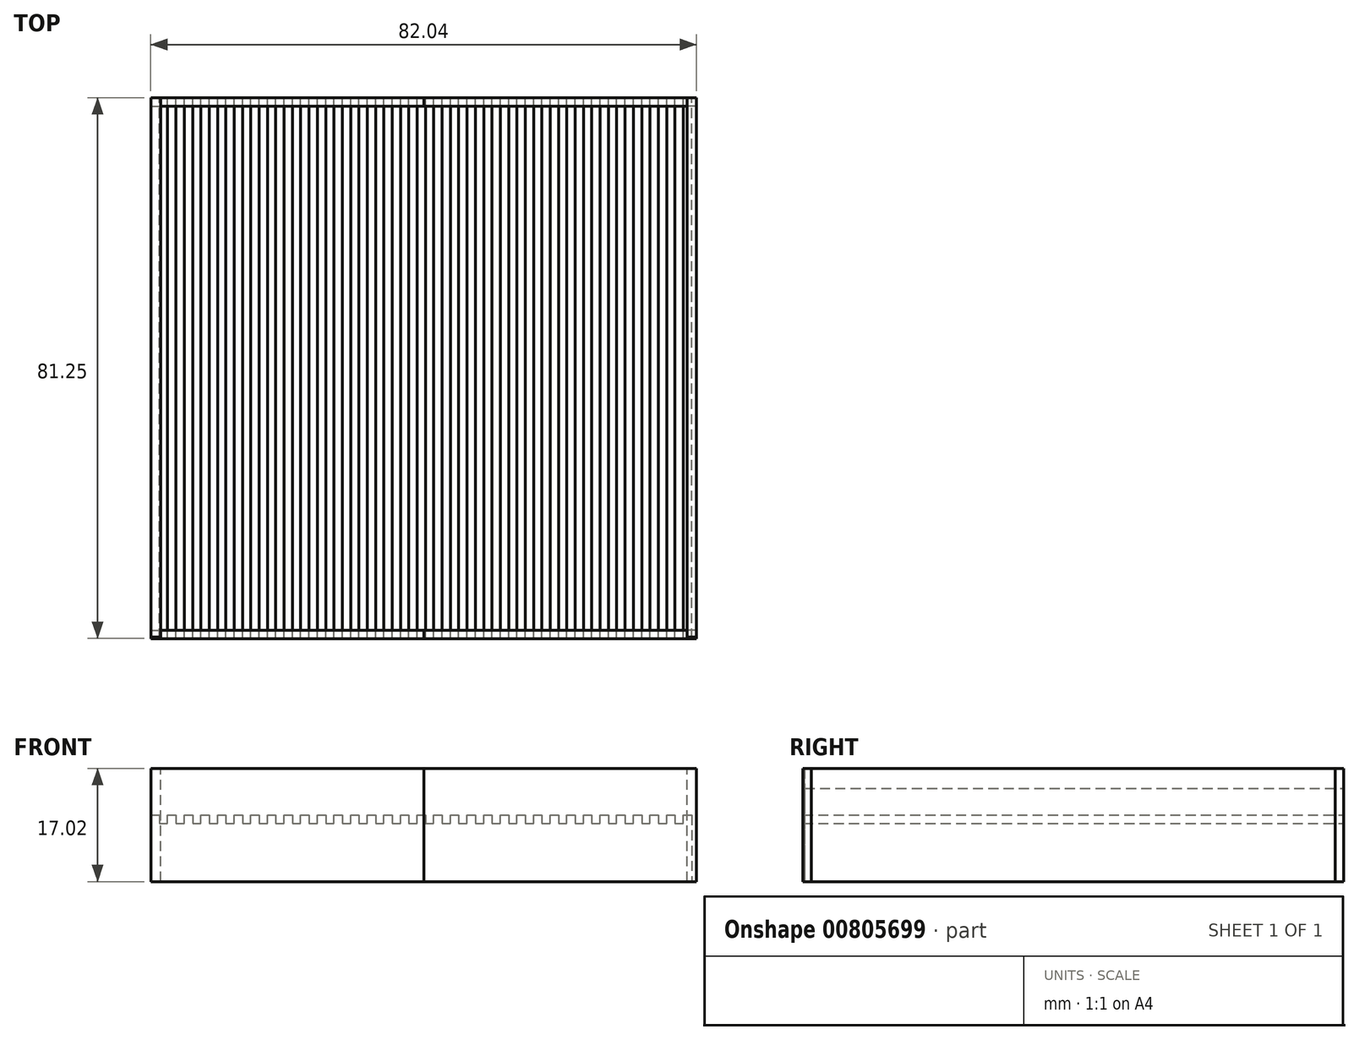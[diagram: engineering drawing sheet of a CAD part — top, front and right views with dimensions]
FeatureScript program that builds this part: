
annotation { "Feature Type Name" : "Feature", "Feature Type Description" : "" }
export const myFeature = defineFeature(function(context is Context, id is Id, definition is map)
    precondition{}
    {
        {
            var Q0;
            Q0=qCreatedBy(makeId("Front.planeOp"),FACE);
            var sketch = newSketch(context, id + "F0", { "sketchPlane" : qUnion([Q0])});
            skLineSegment(sketch, "E0.top", {"start": v(-41, -5) * mm, "end": v(40.25, -5) * mm});
            skLineSegment(sketch, "E0.left", {"start": v(-41, 5) * mm, "end": v(-41, -5) * mm});
            skLineSegment(sketch, "E0.right", {"start": v(40.25, 3.75) * mm, "end": v(40.25, -5) * mm});
            skLineSegment(sketch, "E1", {"start": v(-41, 5) * mm, "end": v(-39.75, 5) * mm});
            skLineSegment(sketch, "E2", {"start": v(-39.75, 5) * mm, "end": v(-39.75, 3.75) * mm});
            skLineSegment(sketch, "E3", {"start": v(-39.75, 3.75) * mm, "end": v(-38.5, 3.75) * mm});
            skLineSegment(sketch, "E4", {"start": v(-38.5, 3.75) * mm, "end": v(-38.5, 5) * mm});
            skLineSegment(sketch, "E5.1.0.0", {"start": v(-36, 3.75) * mm, "end": v(-36, 5) * mm});
            skLineSegment(sketch, "E5.1.0.1", {"start": v(-37.25, 3.75) * mm, "end": v(-36, 3.75) * mm});
            skLineSegment(sketch, "E5.1.0.2", {"start": v(-37.25, 5) * mm, "end": v(-37.25, 3.75) * mm});
            skLineSegment(sketch, "E5.1.0.3", {"start": v(-38.5, 5) * mm, "end": v(-37.25, 5) * mm});
            skLineSegment(sketch, "E5.2.0.0", {"start": v(-33.5, 3.75) * mm, "end": v(-33.5, 5) * mm});
            skLineSegment(sketch, "E5.2.0.1", {"start": v(-34.75, 3.75) * mm, "end": v(-33.5, 3.75) * mm});
            skLineSegment(sketch, "E5.2.0.2", {"start": v(-34.75, 5) * mm, "end": v(-34.75, 3.75) * mm});
            skLineSegment(sketch, "E5.2.0.3", {"start": v(-36, 5) * mm, "end": v(-34.75, 5) * mm});
            skLineSegment(sketch, "E5.3.0.0", {"start": v(-31, 3.75) * mm, "end": v(-31, 5) * mm});
            skLineSegment(sketch, "E5.3.0.1", {"start": v(-32.25, 3.75) * mm, "end": v(-31, 3.75) * mm});
            skLineSegment(sketch, "E5.3.0.2", {"start": v(-32.25, 5) * mm, "end": v(-32.25, 3.75) * mm});
            skLineSegment(sketch, "E5.3.0.3", {"start": v(-33.5, 5) * mm, "end": v(-32.25, 5) * mm});
            skLineSegment(sketch, "E5.4.0.0", {"start": v(-28.5, 3.75) * mm, "end": v(-28.5, 5) * mm});
            skLineSegment(sketch, "E5.4.0.1", {"start": v(-29.75, 3.75) * mm, "end": v(-28.5, 3.75) * mm});
            skLineSegment(sketch, "E5.4.0.2", {"start": v(-29.75, 5) * mm, "end": v(-29.75, 3.75) * mm});
            skLineSegment(sketch, "E5.4.0.3", {"start": v(-31, 5) * mm, "end": v(-29.75, 5) * mm});
            skLineSegment(sketch, "E5.5.0.0", {"start": v(-26, 3.75) * mm, "end": v(-26, 5) * mm});
            skLineSegment(sketch, "E5.5.0.1", {"start": v(-27.25, 3.75) * mm, "end": v(-26, 3.75) * mm});
            skLineSegment(sketch, "E5.5.0.2", {"start": v(-27.25, 5) * mm, "end": v(-27.25, 3.75) * mm});
            skLineSegment(sketch, "E5.5.0.3", {"start": v(-28.5, 5) * mm, "end": v(-27.25, 5) * mm});
            skLineSegment(sketch, "E5.6.0.0", {"start": v(-23.5, 3.75) * mm, "end": v(-23.5, 5) * mm});
            skLineSegment(sketch, "E5.6.0.1", {"start": v(-24.75, 3.75) * mm, "end": v(-23.5, 3.75) * mm});
            skLineSegment(sketch, "E5.6.0.2", {"start": v(-24.75, 5) * mm, "end": v(-24.75, 3.75) * mm});
            skLineSegment(sketch, "E5.6.0.3", {"start": v(-26, 5) * mm, "end": v(-24.75, 5) * mm});
            skLineSegment(sketch, "E5.7.0.0", {"start": v(-21, 3.75) * mm, "end": v(-21, 5) * mm});
            skLineSegment(sketch, "E5.7.0.1", {"start": v(-22.25, 3.75) * mm, "end": v(-21, 3.75) * mm});
            skLineSegment(sketch, "E5.7.0.2", {"start": v(-22.25, 5) * mm, "end": v(-22.25, 3.75) * mm});
            skLineSegment(sketch, "E5.7.0.3", {"start": v(-23.5, 5) * mm, "end": v(-22.25, 5) * mm});
            skLineSegment(sketch, "E5.8.0.0", {"start": v(-18.5, 3.75) * mm, "end": v(-18.5, 5) * mm});
            skLineSegment(sketch, "E5.8.0.1", {"start": v(-19.75, 3.75) * mm, "end": v(-18.5, 3.75) * mm});
            skLineSegment(sketch, "E5.8.0.2", {"start": v(-19.75, 5) * mm, "end": v(-19.75, 3.75) * mm});
            skLineSegment(sketch, "E5.8.0.3", {"start": v(-21, 5) * mm, "end": v(-19.75, 5) * mm});
            skLineSegment(sketch, "E5.9.0.0", {"start": v(-16, 3.75) * mm, "end": v(-16, 5) * mm});
            skLineSegment(sketch, "E5.9.0.1", {"start": v(-17.25, 3.75) * mm, "end": v(-16, 3.75) * mm});
            skLineSegment(sketch, "E5.9.0.2", {"start": v(-17.25, 5) * mm, "end": v(-17.25, 3.75) * mm});
            skLineSegment(sketch, "E5.9.0.3", {"start": v(-18.5, 5) * mm, "end": v(-17.25, 5) * mm});
            skLineSegment(sketch, "E5.10.0.0", {"start": v(-13.5, 3.75) * mm, "end": v(-13.5, 5) * mm});
            skLineSegment(sketch, "E5.10.0.1", {"start": v(-14.75, 3.75) * mm, "end": v(-13.5, 3.75) * mm});
            skLineSegment(sketch, "E5.10.0.2", {"start": v(-14.75, 5) * mm, "end": v(-14.75, 3.75) * mm});
            skLineSegment(sketch, "E5.10.0.3", {"start": v(-16, 5) * mm, "end": v(-14.75, 5) * mm});
            skLineSegment(sketch, "E5.11.0.0", {"start": v(-11, 3.75) * mm, "end": v(-11, 5) * mm});
            skLineSegment(sketch, "E5.11.0.1", {"start": v(-12.25, 3.75) * mm, "end": v(-11, 3.75) * mm});
            skLineSegment(sketch, "E5.11.0.2", {"start": v(-12.25, 5) * mm, "end": v(-12.25, 3.75) * mm});
            skLineSegment(sketch, "E5.11.0.3", {"start": v(-13.5, 5) * mm, "end": v(-12.25, 5) * mm});
            skLineSegment(sketch, "E5.12.0.0", {"start": v(-8.5, 3.75) * mm, "end": v(-8.5, 5) * mm});
            skLineSegment(sketch, "E5.12.0.1", {"start": v(-9.75, 3.75) * mm, "end": v(-8.5, 3.75) * mm});
            skLineSegment(sketch, "E5.12.0.2", {"start": v(-9.75, 5) * mm, "end": v(-9.75, 3.75) * mm});
            skLineSegment(sketch, "E5.12.0.3", {"start": v(-11, 5) * mm, "end": v(-9.75, 5) * mm});
            skLineSegment(sketch, "E5.13.0.0", {"start": v(-6, 3.75) * mm, "end": v(-6, 5) * mm});
            skLineSegment(sketch, "E5.13.0.1", {"start": v(-7.25, 3.75) * mm, "end": v(-6, 3.75) * mm});
            skLineSegment(sketch, "E5.13.0.2", {"start": v(-7.25, 5) * mm, "end": v(-7.25, 3.75) * mm});
            skLineSegment(sketch, "E5.13.0.3", {"start": v(-8.5, 5) * mm, "end": v(-7.25, 5) * mm});
            skLineSegment(sketch, "E5.14.0.0", {"start": v(-3.5, 3.75) * mm, "end": v(-3.5, 5) * mm});
            skLineSegment(sketch, "E5.14.0.1", {"start": v(-4.75, 3.75) * mm, "end": v(-3.5, 3.75) * mm});
            skLineSegment(sketch, "E5.14.0.2", {"start": v(-4.75, 5) * mm, "end": v(-4.75, 3.75) * mm});
            skLineSegment(sketch, "E5.14.0.3", {"start": v(-6, 5) * mm, "end": v(-4.75, 5) * mm});
            skLineSegment(sketch, "E5.15.0.0", {"start": v(-1, 3.75) * mm, "end": v(-1, 5) * mm});
            skLineSegment(sketch, "E5.15.0.1", {"start": v(-2.25, 3.75) * mm, "end": v(-1, 3.75) * mm});
            skLineSegment(sketch, "E5.15.0.2", {"start": v(-2.25, 5) * mm, "end": v(-2.25, 3.75) * mm});
            skLineSegment(sketch, "E5.15.0.3", {"start": v(-3.5, 5) * mm, "end": v(-2.25, 5) * mm});
            skLineSegment(sketch, "E5.16.0.0", {"start": v(1.5, 3.75) * mm, "end": v(1.5, 5) * mm});
            skLineSegment(sketch, "E5.16.0.1", {"start": v(0.25, 3.75) * mm, "end": v(1.5, 3.75) * mm});
            skLineSegment(sketch, "E5.16.0.2", {"start": v(0.25, 5) * mm, "end": v(0.25, 3.75) * mm});
            skLineSegment(sketch, "E5.16.0.3", {"start": v(-1, 5) * mm, "end": v(0.25, 5) * mm});
            skLineSegment(sketch, "E5.17.0.0", {"start": v(4, 3.75) * mm, "end": v(4, 5) * mm});
            skLineSegment(sketch, "E5.17.0.1", {"start": v(2.75, 3.75) * mm, "end": v(4, 3.75) * mm});
            skLineSegment(sketch, "E5.17.0.2", {"start": v(2.75, 5) * mm, "end": v(2.75, 3.75) * mm});
            skLineSegment(sketch, "E5.17.0.3", {"start": v(1.5, 5) * mm, "end": v(2.75, 5) * mm});
            skLineSegment(sketch, "E5.18.0.0", {"start": v(6.5, 3.75) * mm, "end": v(6.5, 5) * mm});
            skLineSegment(sketch, "E5.18.0.1", {"start": v(5.25, 3.75) * mm, "end": v(6.5, 3.75) * mm});
            skLineSegment(sketch, "E5.18.0.2", {"start": v(5.25, 5) * mm, "end": v(5.25, 3.75) * mm});
            skLineSegment(sketch, "E5.18.0.3", {"start": v(4, 5) * mm, "end": v(5.25, 5) * mm});
            skLineSegment(sketch, "E5.19.0.0", {"start": v(9, 3.75) * mm, "end": v(9, 5) * mm});
            skLineSegment(sketch, "E5.19.0.1", {"start": v(7.75, 3.75) * mm, "end": v(9, 3.75) * mm});
            skLineSegment(sketch, "E5.19.0.2", {"start": v(7.75, 5) * mm, "end": v(7.75, 3.75) * mm});
            skLineSegment(sketch, "E5.19.0.3", {"start": v(6.5, 5) * mm, "end": v(7.75, 5) * mm});
            skLineSegment(sketch, "E5.20.0.0", {"start": v(11.5, 3.75) * mm, "end": v(11.5, 5) * mm});
            skLineSegment(sketch, "E5.20.0.1", {"start": v(10.25, 3.75) * mm, "end": v(11.5, 3.75) * mm});
            skLineSegment(sketch, "E5.20.0.2", {"start": v(10.25, 5) * mm, "end": v(10.25, 3.75) * mm});
            skLineSegment(sketch, "E5.20.0.3", {"start": v(9, 5) * mm, "end": v(10.25, 5) * mm});
            skLineSegment(sketch, "E5.21.0.0", {"start": v(14, 3.75) * mm, "end": v(14, 5) * mm});
            skLineSegment(sketch, "E5.21.0.1", {"start": v(12.75, 3.75) * mm, "end": v(14, 3.75) * mm});
            skLineSegment(sketch, "E5.21.0.2", {"start": v(12.75, 5) * mm, "end": v(12.75, 3.75) * mm});
            skLineSegment(sketch, "E5.21.0.3", {"start": v(11.5, 5) * mm, "end": v(12.75, 5) * mm});
            skLineSegment(sketch, "E5.22.0.0", {"start": v(16.5, 3.75) * mm, "end": v(16.5, 5) * mm});
            skLineSegment(sketch, "E5.22.0.1", {"start": v(15.25, 3.75) * mm, "end": v(16.5, 3.75) * mm});
            skLineSegment(sketch, "E5.22.0.2", {"start": v(15.25, 5) * mm, "end": v(15.25, 3.75) * mm});
            skLineSegment(sketch, "E5.22.0.3", {"start": v(14, 5) * mm, "end": v(15.25, 5) * mm});
            skLineSegment(sketch, "E5.23.0.0", {"start": v(19, 3.75) * mm, "end": v(19, 5) * mm});
            skLineSegment(sketch, "E5.23.0.1", {"start": v(17.75, 3.75) * mm, "end": v(19, 3.75) * mm});
            skLineSegment(sketch, "E5.23.0.2", {"start": v(17.75, 5) * mm, "end": v(17.75, 3.75) * mm});
            skLineSegment(sketch, "E5.23.0.3", {"start": v(16.5, 5) * mm, "end": v(17.75, 5) * mm});
            skLineSegment(sketch, "E5.24.0.0", {"start": v(21.5, 3.75) * mm, "end": v(21.5, 5) * mm});
            skLineSegment(sketch, "E5.24.0.1", {"start": v(20.25, 3.75) * mm, "end": v(21.5, 3.75) * mm});
            skLineSegment(sketch, "E5.24.0.2", {"start": v(20.25, 5) * mm, "end": v(20.25, 3.75) * mm});
            skLineSegment(sketch, "E5.24.0.3", {"start": v(19, 5) * mm, "end": v(20.25, 5) * mm});
            skLineSegment(sketch, "E5.25.0.0", {"start": v(24, 3.75) * mm, "end": v(24, 5) * mm});
            skLineSegment(sketch, "E5.25.0.1", {"start": v(22.75, 3.75) * mm, "end": v(24, 3.75) * mm});
            skLineSegment(sketch, "E5.25.0.2", {"start": v(22.75, 5) * mm, "end": v(22.75, 3.75) * mm});
            skLineSegment(sketch, "E5.25.0.3", {"start": v(21.5, 5) * mm, "end": v(22.75, 5) * mm});
            skLineSegment(sketch, "E5.26.0.0", {"start": v(26.5, 3.75) * mm, "end": v(26.5, 5) * mm});
            skLineSegment(sketch, "E5.26.0.1", {"start": v(25.25, 3.75) * mm, "end": v(26.5, 3.75) * mm});
            skLineSegment(sketch, "E5.26.0.2", {"start": v(25.25, 5) * mm, "end": v(25.25, 3.75) * mm});
            skLineSegment(sketch, "E5.26.0.3", {"start": v(24, 5) * mm, "end": v(25.25, 5) * mm});
            skLineSegment(sketch, "E5.27.0.0", {"start": v(29, 3.75) * mm, "end": v(29, 5) * mm});
            skLineSegment(sketch, "E5.27.0.1", {"start": v(27.75, 3.75) * mm, "end": v(29, 3.75) * mm});
            skLineSegment(sketch, "E5.27.0.2", {"start": v(27.75, 5) * mm, "end": v(27.75, 3.75) * mm});
            skLineSegment(sketch, "E5.27.0.3", {"start": v(26.5, 5) * mm, "end": v(27.75, 5) * mm});
            skLineSegment(sketch, "E5.28.0.0", {"start": v(31.5, 3.75) * mm, "end": v(31.5, 5) * mm});
            skLineSegment(sketch, "E5.28.0.1", {"start": v(30.25, 3.75) * mm, "end": v(31.5, 3.75) * mm});
            skLineSegment(sketch, "E5.28.0.2", {"start": v(30.25, 5) * mm, "end": v(30.25, 3.75) * mm});
            skLineSegment(sketch, "E5.28.0.3", {"start": v(29, 5) * mm, "end": v(30.25, 5) * mm});
            skLineSegment(sketch, "E5.29.0.0", {"start": v(34, 3.75) * mm, "end": v(34, 5) * mm});
            skLineSegment(sketch, "E5.29.0.1", {"start": v(32.75, 3.75) * mm, "end": v(34, 3.75) * mm});
            skLineSegment(sketch, "E5.29.0.2", {"start": v(32.75, 5) * mm, "end": v(32.75, 3.75) * mm});
            skLineSegment(sketch, "E5.29.0.3", {"start": v(31.5, 5) * mm, "end": v(32.75, 5) * mm});
            skLineSegment(sketch, "E5.30.0.0", {"start": v(36.5, 3.75) * mm, "end": v(36.5, 5) * mm});
            skLineSegment(sketch, "E5.30.0.1", {"start": v(35.25, 3.75) * mm, "end": v(36.5, 3.75) * mm});
            skLineSegment(sketch, "E5.30.0.2", {"start": v(35.25, 5) * mm, "end": v(35.25, 3.75) * mm});
            skLineSegment(sketch, "E5.30.0.3", {"start": v(34, 5) * mm, "end": v(35.25, 5) * mm});
            skLineSegment(sketch, "E5.31.0.0", {"start": v(39, 3.75) * mm, "end": v(39, 5) * mm});
            skLineSegment(sketch, "E5.31.0.1", {"start": v(37.75, 3.75) * mm, "end": v(39, 3.75) * mm});
            skLineSegment(sketch, "E5.31.0.2", {"start": v(37.75, 5) * mm, "end": v(37.75, 3.75) * mm});
            skLineSegment(sketch, "E5.31.0.3", {"start": v(36.5, 5) * mm, "end": v(37.75, 5) * mm});
            skLineSegment(sketch, "E5.direction1", {"start": v(-38.5, 3.75) * mm, "end": v(-36, 3.75) * mm, "construction": true});
            skLineSegment(sketch, "E6.3.32.0", {"start": v(40.25, 3.75) * mm, "end": v(40.25, 3.75) * mm});
            skLineSegment(sketch, "E6.6.32.0", {"start": v(40.25, 5) * mm, "end": v(40.25, 3.75) * mm});
            skLineSegment(sketch, "E6.9.32.0", {"start": v(39, 5) * mm, "end": v(40.25, 5) * mm});
            skSolve(sketch);
        }
        {
            var Q0;
            Q0=qSketchRegion(id+"F0",true);
            extrude(context, id + "F1", {"entities" : qUnion([Q0]), "depth" : 81.25 * mm, "offsetDistance" : 25 * mm});
        }
        {
            var Q0;
            Q0=qCreatedBy(makeId("Right.planeOp"),FACE);
            var sketch = newSketch(context, id + "F2", { "sketchPlane" : qUnion([Q0])});
            skLineSegment(sketch, "E7", {"start": v(0, 0) * mm, "end": v(0, -5) * mm});
            skLineSegment(sketch, "E8", {"start": v(0, -5) * mm, "end": v(0, 9) * mm});
            skLineSegment(sketch, "E9", {"start": v(0, 9) * mm, "end": v(-1.25, 9) * mm});
            skLineSegment(sketch, "E10", {"start": v(-1.25, 9) * mm, "end": v(-1.25, -5) * mm});
            skLineSegment(sketch, "E11", {"start": v(-1.25, -5) * mm, "end": v(0, -5) * mm});
            skLineSegment(sketch, "E12", {"start": v(0, 0) * mm, "end": v(-85.92, 0) * mm});
            skLineSegment(sketch, "E13", {"start": v(-81.25, 0) * mm, "end": v(-81.25, -5) * mm});
            skLineSegment(sketch, "E14", {"start": v(-81.25, -5) * mm, "end": v(-81.25, 9) * mm});
            skLineSegment(sketch, "E15", {"start": v(-81.25, -5) * mm, "end": v(-80, -5) * mm});
            skLineSegment(sketch, "E16", {"start": v(-80, -5) * mm, "end": v(-80, 9) * mm});
            skLineSegment(sketch, "E17", {"start": v(-80, 9) * mm, "end": v(-81.25, 9) * mm});
            skLineSegment(sketch, "E18", {"start": v(-80, 9) * mm, "end": v(-80, 12) * mm});
            skLineSegment(sketch, "E19", {"start": v(-80, 12) * mm, "end": v(-81.25, 12) * mm});
            skLineSegment(sketch, "E20", {"start": v(-81.25, 12) * mm, "end": v(-81.25, 9) * mm});
            skLineSegment(sketch, "E21", {"start": v(0, 9) * mm, "end": v(0, 12) * mm});
            skLineSegment(sketch, "E22", {"start": v(0, 12) * mm, "end": v(-1.25, 12) * mm});
            skLineSegment(sketch, "E23", {"start": v(-1.25, 12) * mm, "end": v(-1.25, 9) * mm});
            skSolve(sketch);
        }
        {
            var Q0;
            Q0=qSketchRegion(id+"F2",true);
            extrude(context, id + "F3", {"entities" : qUnion([Q0]), "depth" : 41 * mm, "offsetDistance" : 25 * mm});
        }
        {
            var Q0;
            Q0=qSketchRegion(id+"F2",true);
            extrude(context, id + "F4", {"entities" : qUnion([Q0]), "oppositeDirection" : true, "depth" : 41 * mm, "offsetDistance" : 25 * mm});
        }
        {
            var Q0;
            Q0=qCreatedBy(makeId("Front.planeOp"),FACE);
            var sketch = newSketch(context, id + "F5", { "sketchPlane" : qUnion([Q0])});
            skLineSegment(sketch, "E24", {"start": v(-41, 9) * mm, "end": v(-41, -5) * mm});
            skLineSegment(sketch, "E25", {"start": v(-41, -5) * mm, "end": v(-39.58, -5) * mm});
            skLineSegment(sketch, "E26", {"start": v(-39.58, -5) * mm, "end": v(-39.58, 9.02) * mm});
            skLineSegment(sketch, "E27", {"start": v(-39.58, 9.02) * mm, "end": v(-41, 9) * mm});
            skLineSegment(sketch, "E28.MirrorCS", {"start": v(39.58, 9.02) * mm, "end": v(41, 9) * mm});
            skLineSegment(sketch, "E29.MirrorCS", {"start": v(39.58, -5) * mm, "end": v(39.58, 9.02) * mm});
            skLineSegment(sketch, "E30.MirrorCS", {"start": v(41, -5) * mm, "end": v(39.58, -5) * mm});
            skLineSegment(sketch, "E31.MirrorCS", {"start": v(41, 9) * mm, "end": v(41, -5) * mm});
            skLineSegment(sketch, "E32", {"start": v(-41, 9) * mm, "end": v(-41.04, 12) * mm});
            skLineSegment(sketch, "E33", {"start": v(-41.04, 12) * mm, "end": v(-39.58, 12.02) * mm});
            skLineSegment(sketch, "E34", {"start": v(-39.58, 12.02) * mm, "end": v(-39.58, 9.02) * mm});
            skLineSegment(sketch, "E35", {"start": v(41, 9) * mm, "end": v(39.58, 9.02) * mm});
            skLineSegment(sketch, "E36", {"start": v(39.58, 9.02) * mm, "end": v(39.58, 12.02) * mm});
            skLineSegment(sketch, "E37", {"start": v(39.58, 12.02) * mm, "end": v(41, 12.02) * mm});
            skLineSegment(sketch, "E38", {"start": v(41, 12.02) * mm, "end": v(41, 9) * mm});
            skSolve(sketch);
        }
        {
            var Q0;
            Q0 = qSketchRegion(id + "F5", true);
            extrude(context, id + "F6", {"entities" : qUnion([Q0]), "depth" : 81 * mm, "offsetDistance" : 25 * mm});
        }
    });
